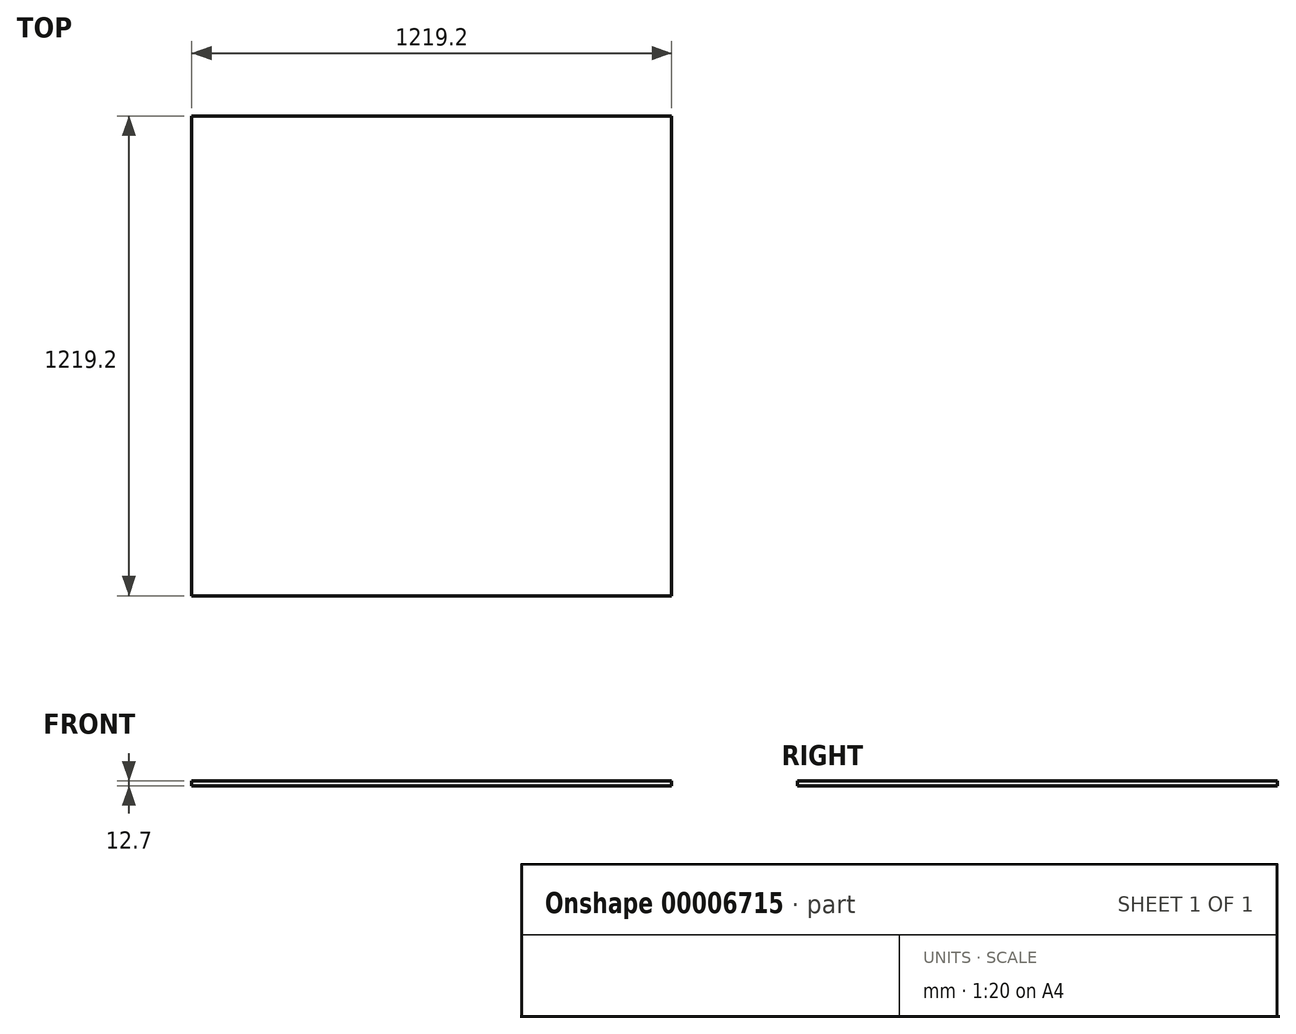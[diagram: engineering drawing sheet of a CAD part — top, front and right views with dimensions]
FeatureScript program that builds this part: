
annotation { "Feature Type Name" : "Feature", "Feature Type Description" : "" }
export const myFeature = defineFeature(function(context is Context, id is Id, definition is map)
    precondition{}
    {
        {
            var Q0;
            Q0=qCreatedBy(makeId("Top.planeOp"),FACE);
            var sketch = newSketch(context, id + "F0", { "sketchPlane" : qUnion([Q0])});
            skLineSegment(sketch, "E0.bottom", {"start": v(-609.6, 609.6) * mm, "end": v(609.6, 609.6) * mm});
            skLineSegment(sketch, "E0.top", {"start": v(-609.6, -609.6) * mm, "end": v(609.6, -609.6) * mm});
            skLineSegment(sketch, "E0.left", {"start": v(-609.6, 609.6) * mm, "end": v(-609.6, -609.6) * mm});
            skLineSegment(sketch, "E0.right", {"start": v(609.6, 609.6) * mm, "end": v(609.6, -609.6) * mm});
            skSolve(sketch);
        }
        {
            var Q0;
            Q0 = qSketchRegion(id + "F0", true);
            extrude(context, id + "F1", {"entities" : qUnion([Q0]), "depth" : 12.7 * mm});
        }
    });
